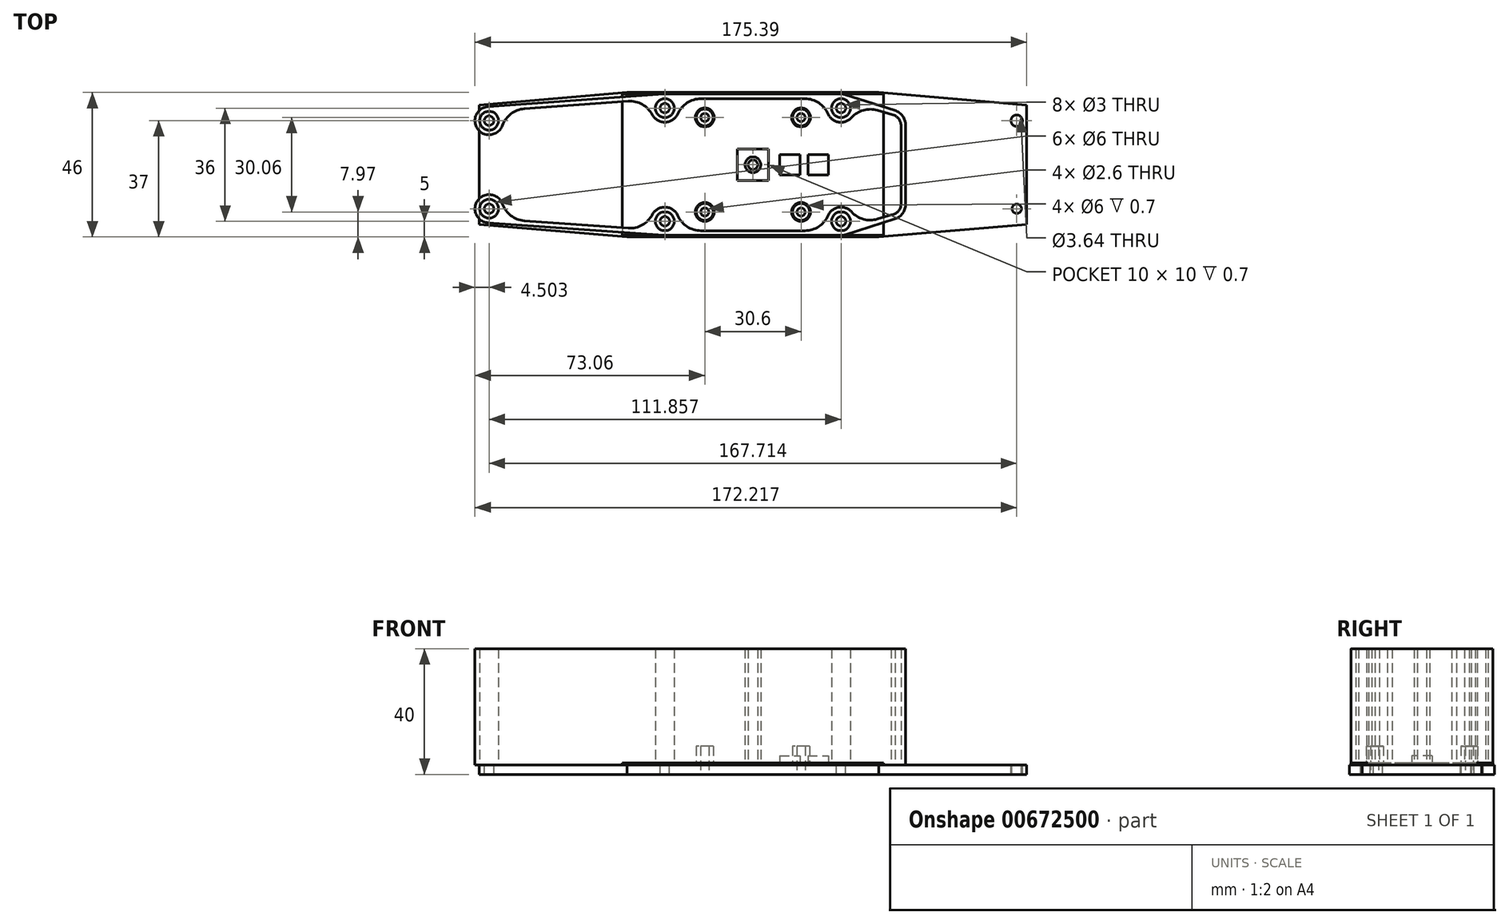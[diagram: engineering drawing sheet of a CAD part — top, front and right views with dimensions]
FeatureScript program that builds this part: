
annotation { "Feature Type Name" : "Feature", "Feature Type Description" : "" }
export const myFeature = defineFeature(function(context is Context, id is Id, definition is map)
    precondition{}
    {
        {
            var Q0;
            Q0=qCreatedBy(makeId("Top.planeOp"),FACE);
            var sketch = newSketch(context, id + "F0", { "sketchPlane" : qUnion([Q0])});
            skLineSegment(sketch, "E0.bottom", {"start": v(-40, 23) * mm, "end": v(40, 23) * mm});
            skLineSegment(sketch, "E0.top", {"start": v(-40, -23) * mm, "end": v(40, -23) * mm});
            skLineSegment(sketch, "E0.left", {"start": v(-40, 23) * mm, "end": v(-40, -23) * mm, "construction": true});
            skLineSegment(sketch, "E0.right", {"start": v(40, 23) * mm, "end": v(40, -23) * mm, "construction": true});
            skCircle(sketch, "E1", {"center": v(-28, 18) * mm, "radius": 1.5 * mm});
            skCircle(sketch, "E2", {"center": v(28, 18) * mm, "radius": 1.5 * mm});
            skCircle(sketch, "E3", {"center": v(-28, -18) * mm, "radius": 1.5 * mm});
            skCircle(sketch, "E4", {"center": v(28, -18) * mm, "radius": 1.5 * mm});
            skCircle(sketch, "E5", {"center": v(-15.3, 15.03) * mm, "radius": 2.7 * mm});
            skCircle(sketch, "E6", {"center": v(15.3, 15.03) * mm, "radius": 2.7 * mm});
            skCircle(sketch, "E7", {"center": v(-15.3, -15.03) * mm, "radius": 2.7 * mm});
            skCircle(sketch, "E8", {"center": v(15.3, -15.03) * mm, "radius": 2.7 * mm});
            skCircle(sketch, "E9", {"center": v(-15.3, 15.03) * mm, "radius": 1.3 * mm});
            skCircle(sketch, "E10", {"center": v(15.3, 15.03) * mm, "radius": 1.3 * mm});
            skCircle(sketch, "E11", {"center": v(15.3, -15.03) * mm, "radius": 1.3 * mm});
            skCircle(sketch, "E12", {"center": v(-15.3, -15.03) * mm, "radius": 1.3 * mm});
            skLineSegment(sketch, "E13", {"start": v(-40, 23) * mm, "end": v(40, -23) * mm, "construction": true});
            skCircle(sketch, "E14", {"center": v(-83.86, 14) * mm, "radius": 1.5 * mm});
            skCircle(sketch, "E15", {"center": v(-83.86, -14) * mm, "radius": 1.5 * mm});
            skCircle(sketch, "E16", {"center": v(83.86, 14) * mm, "radius": 1.82 * mm});
            skCircle(sketch, "E17", {"center": v(83.86, -14) * mm, "radius": 1.5 * mm});
            skLineSegment(sketch, "E18", {"start": v(-40, 23) * mm, "end": v(-87.03, 19) * mm});
            skLineSegment(sketch, "E19", {"start": v(-87.03, 19) * mm, "end": v(-87.03, -19) * mm});
            skLineSegment(sketch, "E20", {"start": v(-87.03, -19) * mm, "end": v(-40, -23) * mm});
            skLineSegment(sketch, "E21", {"start": v(40, 23) * mm, "end": v(87.03, 19) * mm});
            skLineSegment(sketch, "E22", {"start": v(87.03, 19) * mm, "end": v(87.03, -19) * mm});
            skLineSegment(sketch, "E23", {"start": v(87.03, -19) * mm, "end": v(40, -23) * mm});
            skSolve(sketch);
        }
        {
            var Q0;
            Q0=makeQuery(id+"F0.imprint","IMPRINT",FACE,{"disambiguationData":[TD([[makeQuery(id+"F0.imprint","IMPRINT",EDGE,{"derivedFrom":sQuery(id+"F0.wireOp",EDGE,"E0.bottom")}),-1.0]])]});
            extrude(context, id + "F1", {"entities" : qUnion([Q0]), "depth" : -3 * mm, "offsetDistance" : 25 * mm});
        }
        {
            var Q0;
            Q0=makeQuery(id+"F0.imprint","IMPRINT",FACE,{"disambiguationData":[TD([[makeQuery(id+"F0.imprint","IMPRINT",EDGE,{"derivedFrom":sQuery(id+"F0.wireOp",EDGE,"E5")}),1.0]])]});
            extrude(context, id + "F2", {"entities" : qUnion([Q0]), "operationType" : NewBodyOperationType.ADD, "depth" : 6 * mm, "offsetDistance" : 25 * mm, "hasSecondDirection" : true, "secondDirectionOppositeDirection" : true, "secondDirectionDepth" : 3 * mm});
        }
        {
            var Q0;
            Q0=makeQuery(id+"F0.imprint","IMPRINT",FACE,{"disambiguationData":[TD([[makeQuery(id+"F0.imprint","IMPRINT",EDGE,{"derivedFrom":sQuery(id+"F0.wireOp",EDGE,"E6")}),1.0]])]});
            extrude(context, id + "F3", {"entities" : qUnion([Q0]), "operationType" : NewBodyOperationType.ADD, "depth" : 6 * mm, "offsetDistance" : 25 * mm, "hasSecondDirection" : true, "secondDirectionOppositeDirection" : true, "secondDirectionDepth" : 3 * mm});
        }
        {
            var Q0;
            Q0=makeQuery(id+"F0.imprint","IMPRINT",FACE,{"disambiguationData":[TD([[makeQuery(id+"F0.imprint","IMPRINT",EDGE,{"derivedFrom":sQuery(id+"F0.wireOp",EDGE,"E7")}),1.0]])]});
            extrude(context, id + "F4", {"entities" : qUnion([Q0]), "operationType" : NewBodyOperationType.ADD, "depth" : 6 * mm, "offsetDistance" : 25 * mm, "hasSecondDirection" : true, "secondDirectionOppositeDirection" : true, "secondDirectionDepth" : 3 * mm});
        }
        {
            var Q0;
            Q0=makeQuery(id+"F0.imprint","IMPRINT",FACE,{"disambiguationData":[TD([[makeQuery(id+"F0.imprint","IMPRINT",EDGE,{"derivedFrom":sQuery(id+"F0.wireOp",EDGE,"E8")}),1.0]])]});
            extrude(context, id + "F5", {"entities" : qUnion([Q0]), "operationType" : NewBodyOperationType.ADD, "depth" : 6 * mm, "offsetDistance" : 25 * mm, "hasSecondDirection" : true, "secondDirectionOppositeDirection" : true, "secondDirectionDepth" : 3 * mm});
        }
        {
            var Q0;
            Q0=qCreatedBy(makeId("Top.planeOp"),FACE);
            var sketch = newSketch(context, id + "F6", { "sketchPlane" : qUnion([Q0])});
            skLineSegment(sketch, "E24.bottom", {"start": v(-41.5, 22.5) * mm, "end": v(41.5, 22.5) * mm});
            skLineSegment(sketch, "E24.top", {"start": v(-41.5, -22.5) * mm, "end": v(41.5, -22.5) * mm});
            skLineSegment(sketch, "E24.left", {"start": v(-41.5, 22.5) * mm, "end": v(-41.5, -22.5) * mm});
            skLineSegment(sketch, "E24.right", {"start": v(41.5, 22.5) * mm, "end": v(41.5, -22.5) * mm});
            skLineSegment(sketch, "E25", {"start": v(-41.5, 22.5) * mm, "end": v(41.5, -22.5) * mm, "construction": true});
            skCircle(sketch, "E26", {"center": v(-28, 18) * mm, "radius": 1.5 * mm});
            skCircle(sketch, "E27", {"center": v(28, 18) * mm, "radius": 1.5 * mm});
            skCircle(sketch, "E28", {"center": v(28, -18) * mm, "radius": 1.5 * mm});
            skCircle(sketch, "E29", {"center": v(-28, -18) * mm, "radius": 1.5 * mm});
            skCircle(sketch, "E30", {"center": v(-15.3, 15.03) * mm, "radius": 3 * mm});
            skCircle(sketch, "E31", {"center": v(15.3, 15.03) * mm, "radius": 3 * mm});
            skCircle(sketch, "E32", {"center": v(15.3, -15.03) * mm, "radius": 3 * mm});
            skCircle(sketch, "E33", {"center": v(-15.3, -15.03) * mm, "radius": 3 * mm});
            skLineSegment(sketch, "E34.bottom", {"start": v(-5, 5) * mm, "end": v(5, 5) * mm});
            skLineSegment(sketch, "E34.top", {"start": v(-5, -5) * mm, "end": v(5, -5) * mm});
            skLineSegment(sketch, "E34.left", {"start": v(-5, 5) * mm, "end": v(-5, -5) * mm});
            skLineSegment(sketch, "E34.right", {"start": v(5, 5) * mm, "end": v(5, -5) * mm});
            skLineSegment(sketch, "E35.bottom", {"start": v(8.5, 3.25) * mm, "end": v(15, 3.25) * mm});
            skLineSegment(sketch, "E35.top", {"start": v(8.5, -3.25) * mm, "end": v(15, -3.25) * mm});
            skLineSegment(sketch, "E35.left", {"start": v(8.5, 3.25) * mm, "end": v(8.5, -3.25) * mm});
            skLineSegment(sketch, "E35.right", {"start": v(15, 3.25) * mm, "end": v(15, -3.25) * mm});
            skLineSegment(sketch, "E36.bottom", {"start": v(17.5, 3.25) * mm, "end": v(24, 3.25) * mm});
            skLineSegment(sketch, "E36.top", {"start": v(17.5, -3.25) * mm, "end": v(24, -3.25) * mm});
            skLineSegment(sketch, "E36.left", {"start": v(17.5, 3.25) * mm, "end": v(17.5, -3.25) * mm});
            skLineSegment(sketch, "E36.right", {"start": v(24, 3.25) * mm, "end": v(24, -3.25) * mm});
            skSolve(sketch);
        }
        {
            var Q0;
            Q0=makeQuery(id+"F6.imprint","IMPRINT",FACE,{"disambiguationData":[TD([[makeQuery(id+"F6.imprint","IMPRINT",EDGE,{"derivedFrom":sQuery(id+"F6.wireOp",EDGE,"E24.bottom")}),-1.0]])]});
            extrude(context, id + "F7", {"entities" : qUnion([Q0]), "depth" : 0.7 * mm, "offsetDistance" : 25 * mm});
        }
        {
            var Q0;
            Q0=makeQuery(id+"F6.imprint","IMPRINT",FACE,{"disambiguationData":[TD([[makeQuery(id+"F6.imprint","IMPRINT",EDGE,{"derivedFrom":sQuery(id+"F6.wireOp",EDGE,"E35.bottom")}),-1.0]])]});
            extrude(context, id + "F8", {"entities" : qUnion([Q0]), "operationType" : NewBodyOperationType.ADD, "depth" : 3 * mm, "offsetDistance" : 25 * mm});
        }
        {
            var Q0;
            Q0=makeQuery(id+"F6.imprint","IMPRINT",FACE,{"disambiguationData":[TD([[makeQuery(id+"F6.imprint","IMPRINT",EDGE,{"derivedFrom":sQuery(id+"F6.wireOp",EDGE,"E36.bottom")}),-1.0]])]});
            extrude(context, id + "F9", {"entities" : qUnion([Q0]), "operationType" : NewBodyOperationType.ADD, "depth" : 3 * mm, "offsetDistance" : 25 * mm});
        }
        {
            var Q0;
            Q0=qCreatedBy(makeId("Top.planeOp"),FACE);
            var sketch = newSketch(context, id + "F10", { "sketchPlane" : qUnion([Q0])});
            skCircle(sketch, "E37", {"center": v(0, 0) * mm, "radius": 2.5 * mm});
            skCircle(sketch, "E38", {"center": v(0, 0) * mm, "radius": 1.5 * mm});
            skSolve(sketch);
        }
        {
            var Q0;
            Q0=makeQuery(id+"F10.imprint","IMPRINT",FACE,{"disambiguationData":[TD([[makeQuery(id+"F10.imprint","IMPRINT",EDGE,{"derivedFrom":sQuery(id+"F10.wireOp",EDGE,"E37")}),1.0]])]});
            extrude(context, id + "F11", {"entities" : qUnion([Q0]), "depth" : 37 * mm, "offsetDistance" : 25 * mm});
        }
        {
            var Q0;
            Q0=qCreatedBy(makeId("Top.planeOp"),FACE);
            var sketch = newSketch(context, id + "F12", { "sketchPlane" : qUnion([Q0])});
            skArc(sketch, "E39", {"start": v(-31.99, 15.91) * mm, "mid": v(-26.92, 13.63) * mm, "end": v(-23.5, 18) * mm});
            skArc(sketch, "E40", {"start": v(23.88, 16.2) * mm, "mid": v(27.28, 13.56) * mm, "end": v(31.34, 14.99) * mm});
            skArc(sketch, "E41", {"start": v(-28, 22.5) * mm, "mid": v(-28.16, 22.5) * mm, "end": v(-28.32, 22.49) * mm});
            skArc(sketch, "E42", {"start": v(31.34, -14.99) * mm, "mid": v(27.28, -13.56) * mm, "end": v(23.88, -16.2) * mm});
            skArc(sketch, "E43", {"start": v(-23.88, -16.2) * mm, "mid": v(-27.84, -13.5) * mm, "end": v(-31.99, -15.91) * mm});
            skLineSegment(sketch, "E44", {"start": v(-28, 22.5) * mm, "end": v(28, 22.5) * mm});
            skLineSegment(sketch, "E45", {"start": v(-28, -22.5) * mm, "end": v(28, -22.5) * mm});
            skLineSegment(sketch, "E46", {"start": v(-28.32, 22.49) * mm, "end": v(-84.18, 18.49) * mm});
            skLineSegment(sketch, "E47", {"start": v(-84.18, 18.49) * mm, "end": v(-82.83, 18.38) * mm});
            skLineSegment(sketch, "E48", {"start": v(-84.18, -18.49) * mm, "end": v(-28.32, -22.49) * mm});
            skLineSegment(sketch, "E49", {"start": v(-84.18, -18.49) * mm, "end": v(-85.06, -18.34) * mm});
            skArc(sketch, "E50", {"start": v(-82.83, 18.38) * mm, "mid": v(-87.8, 11.84) * mm, "end": v(-79.61, 12.5) * mm});
            skArc(sketch, "E51", {"start": v(-79.61, -12.5) * mm, "mid": v(-87.44, -11.27) * mm, "end": v(-84.18, -18.49) * mm});
            skLineSegment(sketch, "E52", {"start": v(48.56, 12.5) * mm, "end": v(48.56, -12.5) * mm});
            skLineSegment(sketch, "E53", {"start": v(29.37, 22.29) * mm, "end": v(45.09, 17.26) * mm});
            skLineSegment(sketch, "E54", {"start": v(45.09, -17.26) * mm, "end": v(29.37, -22.29) * mm});
            skLineSegment(sketch, "E55", {"start": v(-16.54, 21) * mm, "end": v(16.54, 21) * mm});
            skArc(sketch, "E56", {"start": v(-16.54, 21) * mm, "mid": v(-20.93, 19.7) * mm, "end": v(-23.88, 16.2) * mm});
            skArc(sketch, "E57", {"start": v(23.88, 16.2) * mm, "mid": v(20.93, 19.7) * mm, "end": v(16.54, 21) * mm});
            skLineSegment(sketch, "E58", {"start": v(-72.64, 17.81) * mm, "end": v(-39.64, 20.17) * mm});
            skArc(sketch, "E59", {"start": v(-31.99, 15.91) * mm, "mid": v(-35.18, 19.18) * mm, "end": v(-39.64, 20.17) * mm});
            skArc(sketch, "E60", {"start": v(-72.64, 17.81) * mm, "mid": v(-76.92, 16.2) * mm, "end": v(-79.61, 12.5) * mm});
            skArc(sketch, "E61", {"start": v(-79.61, -12.5) * mm, "mid": v(-76.92, -16.2) * mm, "end": v(-72.64, -17.81) * mm});
            skArc(sketch, "E62", {"start": v(-39.64, -20.17) * mm, "mid": v(-35.18, -19.18) * mm, "end": v(-31.99, -15.91) * mm});
            skArc(sketch, "E63", {"start": v(-23.88, -16.2) * mm, "mid": v(-20.93, -19.7) * mm, "end": v(-16.54, -21) * mm});
            skArc(sketch, "E64", {"start": v(16.54, -21) * mm, "mid": v(20.93, -19.7) * mm, "end": v(23.88, -16.2) * mm});
            skLineSegment(sketch, "E65", {"start": v(-16.54, -21) * mm, "end": v(16.54, -21) * mm});
            skLineSegment(sketch, "E66", {"start": v(-72.64, -17.81) * mm, "end": v(-39.64, -20.17) * mm});
            skPoint(sketch, "E67.visualSharp", {"position": v(48.56, 16.15) * mm});
            skArc(sketch, "E67.filletArc", {"start": v(48.56, 12.5) * mm, "mid": v(47.6, 15.45) * mm, "end": v(45.09, 17.26) * mm});
            skPoint(sketch, "E68.visualSharp", {"position": v(48.56, -16.15) * mm});
            skArc(sketch, "E68.filletArc", {"start": v(45.09, -17.26) * mm, "mid": v(47.6, -15.45) * mm, "end": v(48.56, -12.5) * mm});
            skArc(sketch, "E69.0", {"start": v(47.06, 12.5) * mm, "mid": v(46.55, 14.32) * mm, "end": v(45.17, 15.61) * mm});
            skLineSegment(sketch, "E69.1", {"start": v(47.06, 12.5) * mm, "end": v(47.06, -12.5) * mm});
            skArc(sketch, "E69.2", {"start": v(43.95, -15.98) * mm, "mid": v(46.17, -14.84) * mm, "end": v(47.06, -12.5) * mm});
            skArc(sketch, "E70", {"start": v(39.6, 17.3) * mm, "mid": v(35.14, 17.34) * mm, "end": v(31.34, 14.99) * mm});
            skArc(sketch, "E71", {"start": v(31.34, -14.99) * mm, "mid": v(35.14, -17.34) * mm, "end": v(39.6, -17.3) * mm});
            skLineSegment(sketch, "E72", {"start": v(45.17, 15.61) * mm, "end": v(39.6, 17.3) * mm});
            skLineSegment(sketch, "E73", {"start": v(43.95, -15.98) * mm, "end": v(39.6, -17.3) * mm});
            skArc(sketch, "E74.trimOffspring", {"start": v(29.37, 22.29) * mm, "mid": v(28.7, 22.45) * mm, "end": v(28, 22.5) * mm});
            skArc(sketch, "E75.trimOffspring", {"start": v(28, -22.5) * mm, "mid": v(28.7, -22.45) * mm, "end": v(29.37, -22.29) * mm});
            skArc(sketch, "E76.trimOffspring", {"start": v(-28.32, -22.49) * mm, "mid": v(-28.16, -22.5) * mm, "end": v(-28, -22.5) * mm});
            skCircle(sketch, "E77", {"center": v(-83.86, -14) * mm, "radius": 3 * mm});
            skCircle(sketch, "E78", {"center": v(-28, -18) * mm, "radius": 3 * mm});
            skCircle(sketch, "E79", {"center": v(-28, 18) * mm, "radius": 3 * mm});
            skCircle(sketch, "E80", {"center": v(28, 18) * mm, "radius": 3 * mm});
            skCircle(sketch, "E81", {"center": v(28, -18) * mm, "radius": 3 * mm});
            skCircle(sketch, "E82", {"center": v(-83.86, 14) * mm, "radius": 3 * mm});
            skSolve(sketch);
        }
        {
            var Q0;
            Q0 = qSketchRegion(id + "F12", true);
            extrude(context, id + "F13", {"entities" : qUnion([Q0]), "depth" : 37 * mm, "offsetDistance" : 25 * mm});
        }
    });
